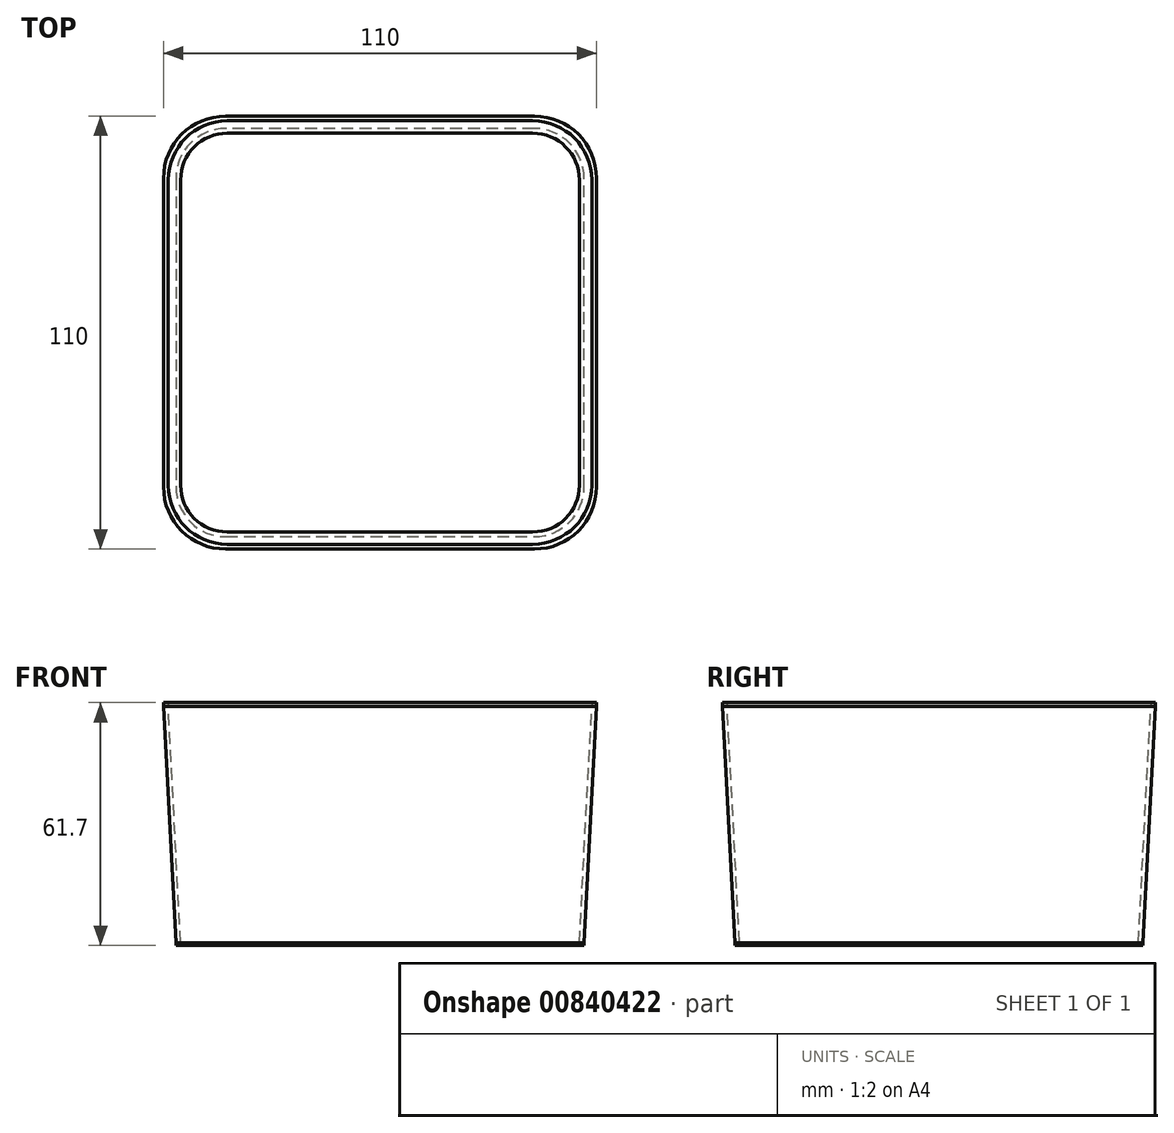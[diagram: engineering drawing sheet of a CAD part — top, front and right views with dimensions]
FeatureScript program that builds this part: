
annotation { "Feature Type Name" : "Feature", "Feature Type Description" : "" }
export const myFeature = defineFeature(function(context is Context, id is Id, definition is map)
    precondition{}
    {
        {
            var Q0;
            Q0=qCreatedBy(makeId("Top.planeOp"),FACE);
            var sketch = newSketch(context, id + "F0", { "sketchPlane" : qUnion([Q0])});
            skLineSegment(sketch, "E0.bottom", {"start": v(-39.2, 55) * mm, "end": v(39.2, 55) * mm});
            skLineSegment(sketch, "E0.top", {"start": v(-39.2, -55) * mm, "end": v(39.2, -55) * mm});
            skLineSegment(sketch, "E0.left", {"start": v(-55, 39.2) * mm, "end": v(-55, -39.2) * mm});
            skLineSegment(sketch, "E0.right", {"start": v(55, 39.2) * mm, "end": v(55, -39.2) * mm});
            skPoint(sketch, "E0.middle", {"position": v(0, 0) * mm});
            skLineSegment(sketch, "E1.bottom", {"start": v(39.2, 65) * mm, "end": v(-39.2, 65) * mm});
            skLineSegment(sketch, "E1.top", {"start": v(39.2, -65) * mm, "end": v(-39.2, -65) * mm});
            skLineSegment(sketch, "E1.left", {"start": v(65, 39.2) * mm, "end": v(65, -39.2) * mm});
            skLineSegment(sketch, "E1.right", {"start": v(-65, 39.2) * mm, "end": v(-65, -39.2) * mm});
            skLineSegment(sketch, "E2.0", {"start": v(-38.8, 53.8) * mm, "end": v(38.8, 53.8) * mm});
            skLineSegment(sketch, "E2.1", {"start": v(-53.8, 38.8) * mm, "end": v(-53.8, -38.8) * mm});
            skLineSegment(sketch, "E2.2", {"start": v(-38.8, -53.8) * mm, "end": v(38.8, -53.8) * mm});
            skLineSegment(sketch, "E2.3", {"start": v(53.8, 38.8) * mm, "end": v(53.8, -38.8) * mm});
            skPoint(sketch, "E3.visualSharp", {"position": v(-53.8, -53.8) * mm});
            skArc(sketch, "E3.filletArc", {"start": v(-53.8, -38.8) * mm, "mid": v(-49.4, -49.4) * mm, "end": v(-38.8, -53.8) * mm});
            skPoint(sketch, "E4.visualSharp", {"position": v(-55, -55) * mm});
            skArc(sketch, "E4.filletArc", {"start": v(-55, -39.2) * mm, "mid": v(-50.37, -50.37) * mm, "end": v(-39.2, -55) * mm});
            skPoint(sketch, "E5.visualSharp", {"position": v(53.8, -53.8) * mm});
            skArc(sketch, "E5.filletArc", {"start": v(38.8, -53.8) * mm, "mid": v(49.4, -49.4) * mm, "end": v(53.8, -38.8) * mm});
            skPoint(sketch, "E6.visualSharp", {"position": v(53.8, 53.8) * mm});
            skArc(sketch, "E6.filletArc", {"start": v(53.8, 38.8) * mm, "mid": v(49.4, 49.4) * mm, "end": v(38.8, 53.8) * mm});
            skPoint(sketch, "E7.visualSharp", {"position": v(-53.8, 53.8) * mm});
            skArc(sketch, "E7.filletArc", {"start": v(-38.8, 53.8) * mm, "mid": v(-49.4, 49.4) * mm, "end": v(-53.8, 38.8) * mm});
            skPoint(sketch, "E8.visualSharp", {"position": v(-55, 55) * mm});
            skArc(sketch, "E8.filletArc", {"start": v(-39.2, 55) * mm, "mid": v(-50.37, 50.37) * mm, "end": v(-55, 39.2) * mm});
            skPoint(sketch, "E9.visualSharp", {"position": v(55, 55) * mm});
            skArc(sketch, "E9.filletArc", {"start": v(55, 39.2) * mm, "mid": v(50.37, 50.37) * mm, "end": v(39.2, 55) * mm});
            skPoint(sketch, "E10.visualSharp", {"position": v(55, -55) * mm});
            skArc(sketch, "E10.filletArc", {"start": v(39.2, -55) * mm, "mid": v(50.37, -50.37) * mm, "end": v(55, -39.2) * mm});
            skPoint(sketch, "E11.visualSharp", {"position": v(65, -65) * mm});
            skArc(sketch, "E11.filletArc", {"start": v(39.2, -65) * mm, "mid": v(57.44, -57.44) * mm, "end": v(65, -39.2) * mm});
            skPoint(sketch, "E12.visualSharp", {"position": v(-65, -65) * mm});
            skArc(sketch, "E12.filletArc", {"start": v(-65, -39.2) * mm, "mid": v(-57.44, -57.44) * mm, "end": v(-39.2, -65) * mm});
            skPoint(sketch, "E13.visualSharp", {"position": v(65, 65) * mm});
            skArc(sketch, "E13.filletArc", {"start": v(65, 39.2) * mm, "mid": v(57.44, 57.44) * mm, "end": v(39.2, 65) * mm});
            skPoint(sketch, "E14.visualSharp", {"position": v(-65, 65) * mm});
            skArc(sketch, "E14.filletArc", {"start": v(-39.2, 65) * mm, "mid": v(-57.44, 57.44) * mm, "end": v(-65, 39.2) * mm});
            skLineSegment(sketch, "E15.0", {"start": v(60, 39.2) * mm, "end": v(60, -39.2) * mm});
            skLineSegment(sketch, "E16.0", {"start": v(-60, 39.2) * mm, "end": v(-60, -39.2) * mm});
            skCircle(sketch, "E17", {"center": v(60, 39.2) * mm, "radius": 2.1 * mm});
            skCircle(sketch, "E18", {"center": v(60, -39.2) * mm, "radius": 2.1 * mm});
            skCircle(sketch, "E19", {"center": v(-60, 39.2) * mm, "radius": 2.1 * mm});
            skCircle(sketch, "E20", {"center": v(-60, -39.2) * mm, "radius": 2.1 * mm});
            skLineSegment(sketch, "E21.0", {"start": v(39.2, 60) * mm, "end": v(-39.2, 60) * mm});
            skCircle(sketch, "E22", {"center": v(-39.2, 60) * mm, "radius": 2.1 * mm});
            skCircle(sketch, "E23", {"center": v(39.2, 60) * mm, "radius": 2.1 * mm});
            skSolve(sketch);
        }
        {
            var Q0;
            Q0=makeQuery(id+"F0.imprint","IMPRINT",FACE,{"disambiguationData":[TD([[makeQuery(id+"F0.imprint","IMPRINT",EDGE,{"derivedFrom":sQuery(id+"F0.wireOp",EDGE,"E0.bottom")}),-1.0]])]});
            extrude(context, id + "F1", {"entities" : qUnion([Q0]), "depth" : 1 * mm, "offsetDistance" : 25 * mm});
        }
        {
            var Q0;
            Q0=makeQuery(id+"F0.imprint","IMPRINT",FACE,{"disambiguationData":[TD([[makeQuery(id+"F0.imprint","IMPRINT",EDGE,{"derivedFrom":sQuery(id+"F0.wireOp",EDGE,"E0.bottom")}),-1.0]])]});
            var Q1;
            Q1=makeQuery(id+"F0.imprint","IMPRINT",FACE,{"disambiguationData":[TD([[makeQuery(id+"F0.imprint","IMPRINT",EDGE,{"derivedFrom":sQuery(id+"F0.wireOp",EDGE,"E2.0")}),-1.0]])]});
            extrude(context, id + "F2", {"entities" : qUnion([Q0, Q1]), "operationType" : NewBodyOperationType.ADD, "oppositeDirection" : true, "depth" : 60 * mm, "offsetDistance" : 25 * mm, "hasDraft" : true, "draftAngle" : 3 * degree, "draftPullDirection" : true});
        }
        {
            var Q0;
            Q0=makeQuery(id+"F0.imprint","IMPRINT",FACE,{"disambiguationData":[TD([[makeQuery(id+"F0.imprint","IMPRINT",EDGE,{"derivedFrom":sQuery(id+"F0.wireOp",EDGE,"E2.0")}),-1.0]])]});
            extrude(context, id + "F3", {"entities" : qUnion([Q0]), "operationType" : NewBodyOperationType.REMOVE, "oppositeDirection" : true, "depth" : 60 * mm, "offsetDistance" : 25 * mm, "hasDraft" : true, "draftAngle" : 3 * degree, "draftPullDirection" : true});
        }
        {
            var Q0;
            Q0=makeQuery(id+"F2.opExtrude","CAP_FACE",FACE,{"disambiguationData":[OSD([sQuery(id+"F0.wireOp",EDGE,"E0.bottom"),sQuery(id+"F0.wireOp",EDGE,"E0.top"),sQuery(id+"F0.wireOp",EDGE,"E0.left"),sQuery(id+"F0.wireOp",EDGE,"E0.right"),sQuery(id+"F0.wireOp",EDGE,"E4.filletArc"),sQuery(id+"F0.wireOp",EDGE,"E8.filletArc"),sQuery(id+"F0.wireOp",EDGE,"E9.filletArc"),sQuery(id+"F0.wireOp",EDGE,"E10.filletArc")])],"isStart":false});
            var sketch = newSketch(context, id + "F4", { "sketchPlane" : qUnion([Q0])});
            skArc(sketch, "E24.0", {"start": v(51.86, -39.2) * mm, "mid": v(48.15, -48.15) * mm, "end": v(39.2, -51.86) * mm});
            skLineSegment(sketch, "E25.0", {"start": v(-39.2, -51.86) * mm, "end": v(39.2, -51.86) * mm});
            skLineSegment(sketch, "E26.0", {"start": v(51.86, -39.2) * mm, "end": v(51.86, 39.2) * mm});
            skArc(sketch, "E27.0", {"start": v(39.2, 51.86) * mm, "mid": v(48.15, 48.15) * mm, "end": v(51.86, 39.2) * mm});
            skLineSegment(sketch, "E28.0", {"start": v(-39.2, 51.86) * mm, "end": v(39.2, 51.86) * mm});
            skArc(sketch, "E29.0", {"start": v(-51.86, 39.2) * mm, "mid": v(-48.15, 48.15) * mm, "end": v(-39.2, 51.86) * mm});
            skLineSegment(sketch, "E30.0", {"start": v(-51.86, -39.2) * mm, "end": v(-51.86, 39.2) * mm});
            skArc(sketch, "E31.0", {"start": v(-39.2, -51.86) * mm, "mid": v(-48.15, -48.15) * mm, "end": v(-51.86, -39.2) * mm});
            skSolve(sketch);
        }
        {
            var Q0;
            Q0=makeQuery(id+"F4.imprint","IMPRINT",FACE,{"disambiguationData":[TD([[makeQuery(id+"F4.imprint","IMPRINT",EDGE,{"derivedFrom":sQuery(id+"F4.wireOp",EDGE,"E24.0")}),-1.0]])]});
            var Q1;
            Q1=makeQuery(id+"F4.imprint","IMPRINT",FACE,{"disambiguationData":[TD([[makeQuery(id+"F4.imprint","IMPRINT",EDGE,{"derivedFrom":makeQuery(id+"F3.boolean.opBoolean","COPY",EDGE,{"derivedFrom":makeQuery(id+"F3.opExtrude","CAP_EDGE",EDGE,{"disambiguationData":[OSD([sQuery(id+"F0.wireOp",EDGE,"E2.0")])],"isStart":false})})}),1.0]])]});
            extrude(context, id + "F5", {"entities" : qUnion([Q0, Q1]), "operationType" : NewBodyOperationType.ADD, "depth" : 0.7 * mm, "offsetDistance" : 25 * mm});
        }
    });
